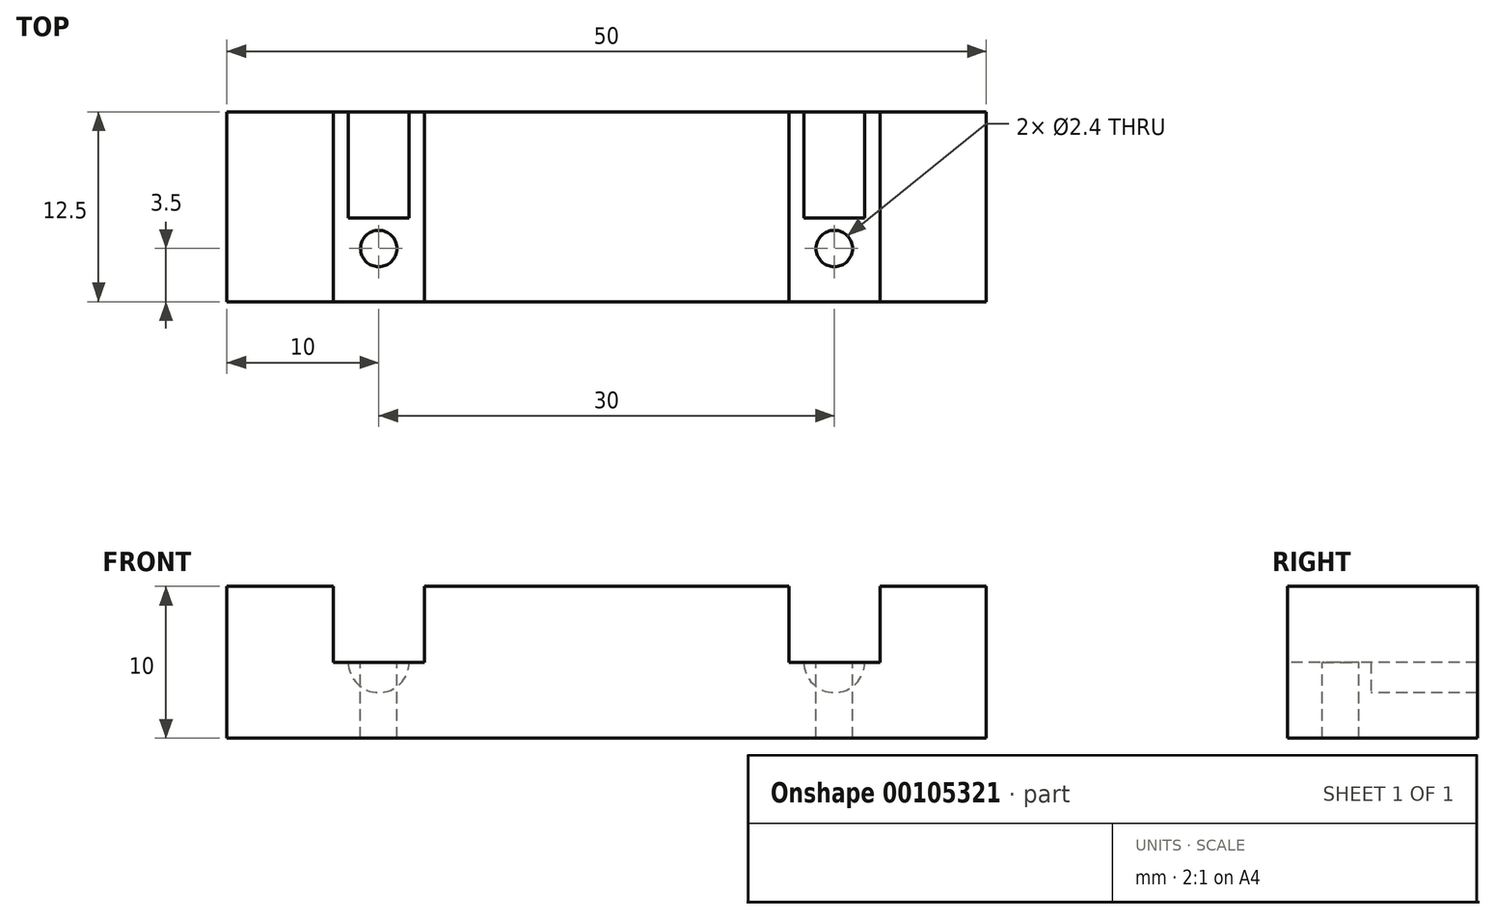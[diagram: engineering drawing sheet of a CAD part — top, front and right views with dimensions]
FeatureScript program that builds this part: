
annotation { "Feature Type Name" : "Feature", "Feature Type Description" : "" }
export const myFeature = defineFeature(function(context is Context, id is Id, definition is map)
    precondition{}
    {
        {
            var Q0;
            Q0=qCreatedBy(makeId("Front.planeOp"),FACE);
            var sketch = newSketch(context, id + "F0", { "sketchPlane" : qUnion([Q0])});
            skLineSegment(sketch, "E0.bottom", {"start": v(25, 5) * mm, "end": v(-25, 5) * mm});
            skLineSegment(sketch, "E0.top", {"start": v(25, -5) * mm, "end": v(-25, -5) * mm});
            skLineSegment(sketch, "E0.left", {"start": v(25, 5) * mm, "end": v(25, -5) * mm});
            skLineSegment(sketch, "E0.right", {"start": v(-25, 5) * mm, "end": v(-25, -5) * mm});
            skPoint(sketch, "E0.middle", {"position": v(0, 0) * mm});
            skSolve(sketch);
        }
        {
            var Q0;
            Q0=makeQuery(id+"F0.imprint","IMPRINT",FACE,{"disambiguationData":[TD([[makeQuery(id+"F0.imprint","IMPRINT",EDGE,{"derivedFrom":sQuery(id+"F0.wireOp",EDGE,"E0.bottom")}),1.0]])]});
            extrude(context, id + "F1", {"entities" : qUnion([Q0]), "depth" : 12.5 * mm});
        }
        {
            var Q0;
            Q0=makeQuery(id+"F1.opExtrude","SWEPT_FACE",FACE,{"disambiguationData":[OSD([sQuery(id+"F0.wireOp",EDGE,"E0.bottom")])]});
            var sketch = newSketch(context, id + "F2", { "sketchPlane" : qUnion([Q0])});
            skLineSegment(sketch, "E1", {"start": v(-15, 5.9) * mm, "end": v(-15, -22.38) * mm, "construction": true});
            skLineSegment(sketch, "E2", {"start": v(0, 18.1) * mm, "end": v(0, -23.6) * mm, "construction": true});
            skPoint(sketch, "E2.endSnap0", {"position": v(0, -12.5) * mm});
            skLineSegment(sketch, "E3.MirrorCS", {"start": v(15, 5.9) * mm, "end": v(15, -22.38) * mm, "construction": true});
            skLineSegment(sketch, "E4.bottom", {"start": v(-12, 3.9) * mm, "end": v(-18, 3.9) * mm});
            skLineSegment(sketch, "E4.top", {"start": v(-12, -15.52) * mm, "end": v(-18, -15.52) * mm});
            skLineSegment(sketch, "E4.left", {"start": v(-12, 3.9) * mm, "end": v(-12, -15.52) * mm});
            skLineSegment(sketch, "E4.right", {"start": v(-18, 3.9) * mm, "end": v(-18, -15.52) * mm});
            skPoint(sketch, "E4.middle", {"position": v(-15, -5.8) * mm});
            skLineSegment(sketch, "E5.bottom", {"start": v(18, 1.62) * mm, "end": v(12, 1.62) * mm});
            skLineSegment(sketch, "E5.top", {"start": v(18, -13.7) * mm, "end": v(12, -13.7) * mm});
            skLineSegment(sketch, "E5.left", {"start": v(18, 1.62) * mm, "end": v(18, -13.7) * mm});
            skLineSegment(sketch, "E5.right", {"start": v(12, 1.62) * mm, "end": v(12, -13.7) * mm});
            skPoint(sketch, "E5.middle", {"position": v(15, -6.04) * mm});
            skSolve(sketch);
        }
        {
            var Q0;
            {var subQ0=sQuery(id+"F2.wireOp",EDGE,"E4.left");var subQ1=sQuery(id+"F0.wireOp",EDGE,"E0.bottom");var subQ2=makeQuery(id+"F1.opExtrude","CAP_EDGE",EDGE,{"disambiguationData":[OSD([subQ1])],"isStart":true});var subQ3=makeQuery(id+"F2.imprint","INTERSECT",VERTEX,{"derivedFrom":[subQ2,subQ0]});Q0=makeQuery(id+"F2.imprint","IMPRINT",FACE,{"disambiguationData":[TD([[makeQuery(id+"F2.imprint","IMPRINT",EDGE,{"disambiguationData":[TD([[subQ3,-1.0]])],"derivedFrom":subQ0}),-1.0]])]});}
            var Q1;
            {var subQ0=sQuery(id+"F2.wireOp",EDGE,"E5.left");var subQ1=sQuery(id+"F0.wireOp",EDGE,"E0.bottom");var subQ2=makeQuery(id+"F1.opExtrude","CAP_EDGE",EDGE,{"disambiguationData":[OSD([subQ1])],"isStart":true});var subQ3=makeQuery(id+"F2.imprint","INTERSECT",VERTEX,{"derivedFrom":[subQ2,subQ0]});Q1=makeQuery(id+"F2.imprint","IMPRINT",FACE,{"disambiguationData":[TD([[makeQuery(id+"F2.imprint","IMPRINT",EDGE,{"disambiguationData":[TD([[subQ3,-1.0]])],"derivedFrom":subQ0}),-1.0]])]});}
            extrude(context, id + "F3", {"entities" : qUnion([Q0, Q1]), "operationType" : NewBodyOperationType.REMOVE, "oppositeDirection" : true, "depth" : 5 * mm});
        }
        {
            var Q0;
            Q0=makeQuery(id+"F3.boolean.opBoolean","COPY",FACE,{"derivedFrom":makeQuery(id+"F3.opExtrude","CAP_FACE",FACE,{"disambiguationData":[OSD([sQuery(id+"F0.wireOp",EDGE,"E0.bottom"),sQuery(id+"F2.wireOp",EDGE,"E4.left"),sQuery(id+"F2.wireOp",EDGE,"E4.right")])],"isStart":false})});
            var sketch = newSketch(context, id + "F4", { "sketchPlane" : qUnion([Q0])});
            skLineSegment(sketch, "E6", {"start": v(-15, 0) * mm, "end": v(-15, -15.32) * mm, "construction": true});
            skPoint(sketch, "E6.endSnap0", {"position": v(-15, 0) * mm});
            skLineSegment(sketch, "E7.bottom", {"start": v(-15, 0) * mm, "end": v(-13, 0) * mm});
            skLineSegment(sketch, "E7.top", {"start": v(-15, -7) * mm, "end": v(-13, -7) * mm});
            skLineSegment(sketch, "E7.left", {"start": v(-15, 0) * mm, "end": v(-15, -7) * mm});
            skLineSegment(sketch, "E7.right", {"start": v(-13, 0) * mm, "end": v(-13, -7) * mm});
            skPoint(sketch, "E8", {"position": v(-15, -9) * mm});
            skSolve(sketch);
        }
        {
            var Q0;
            Q0=makeQuery(id+"F3.boolean.opBoolean","COPY",FACE,{"derivedFrom":makeQuery(id+"F3.opExtrude","CAP_FACE",FACE,{"disambiguationData":[OSD([sQuery(id+"F0.wireOp",EDGE,"E0.bottom"),sQuery(id+"F2.wireOp",EDGE,"E5.left"),sQuery(id+"F2.wireOp",EDGE,"E5.right")])],"isStart":false})});
            var sketch = newSketch(context, id + "F5", { "sketchPlane" : qUnion([Q0])});
            skLineSegment(sketch, "E9", {"start": v(15, 0) * mm, "end": v(15, -18.83) * mm, "construction": true});
            skPoint(sketch, "E9.endSnap0", {"position": v(15, 0) * mm});
            skLineSegment(sketch, "E10.bottom", {"start": v(15, 0) * mm, "end": v(17, 0) * mm});
            skLineSegment(sketch, "E10.top", {"start": v(15, -7) * mm, "end": v(17, -7) * mm});
            skLineSegment(sketch, "E10.left", {"start": v(15, 0) * mm, "end": v(15, -7) * mm});
            skLineSegment(sketch, "E10.right", {"start": v(17, 0) * mm, "end": v(17, -7) * mm});
            skPoint(sketch, "E11", {"position": v(15, -9) * mm});
            skSolve(sketch);
        }
        {
            var Q0;
            Q0=makeQuery(id+"F4.imprint","IMPRINT",FACE,{"disambiguationData":[TD([[makeQuery(id+"F4.imprint","IMPRINT",EDGE,{"derivedFrom":sQuery(id+"F4.wireOp",EDGE,"E7.bottom")}),1.0]])]});
            var Q1;
            Q1=sQuery(id+"F4.wireOp",EDGE,"E6");
            revolve(context, id + "F6", {"operationType" : NewBodyOperationType.REMOVE, "entities" : qUnion([Q0]), "axis" : qUnion([Q1]), "revolveType" : RevolveType.FULL, "oppositeDirection" : true});
        }
        {
            var Q0;
            Q0=makeQuery(id+"F5.imprint","IMPRINT",FACE,{"disambiguationData":[TD([[makeQuery(id+"F5.imprint","IMPRINT",EDGE,{"derivedFrom":sQuery(id+"F5.wireOp",EDGE,"E10.bottom")}),1.0]])]});
            var Q1;
            Q1=sQuery(id+"F5.wireOp",EDGE,"E9");
            revolve(context, id + "F7", {"operationType" : NewBodyOperationType.REMOVE, "entities" : qUnion([Q0]), "axis" : qUnion([Q1]), "revolveType" : RevolveType.FULL});
        }
        {
            var Q0;
            Q0=sQuery(id+"F4.wireOp",VERTEX,"E8");
            var Q1;
            Q1=sQuery(id+"F5.wireOp",VERTEX,"E11");
            var Q2;
            Q2=makeQuery(id+"F1.opExtrude","SWEPT_BODY",BODY,{"disambiguationData":[OSD([sQuery(id+"F0.wireOp",EDGE,"E0.bottom"),sQuery(id+"F0.wireOp",EDGE,"E0.top"),sQuery(id+"F0.wireOp",EDGE,"E0.left"),sQuery(id+"F0.wireOp",EDGE,"E0.right")])]});
            hole(context, id + "F8", {"style" : HoleStyle.SIMPLE, "endStyle" : HoleEndStyle.THROUGH, "standardTappedOrClearance" : lookupTablePath({ "standard" : "ISO", "engagement" : "75%", "pitch" : "0.6 mm", "size" : "M3", "type" : "Tapped" }), "standardBlindInLast" : lookupTablePath({ "standard" : "ISO", "engagement" : "75%", "pitch" : "0.6 mm", "size" : "M3", "type" : "Tapped" }), "holeDiameter" : 2.4 * mm, "locations" : qUnion([Q0, Q1]), "scope" : qUnion([Q2]), "isTappedThrough" : true, "showTappedDepth" : true});
        }
    });
